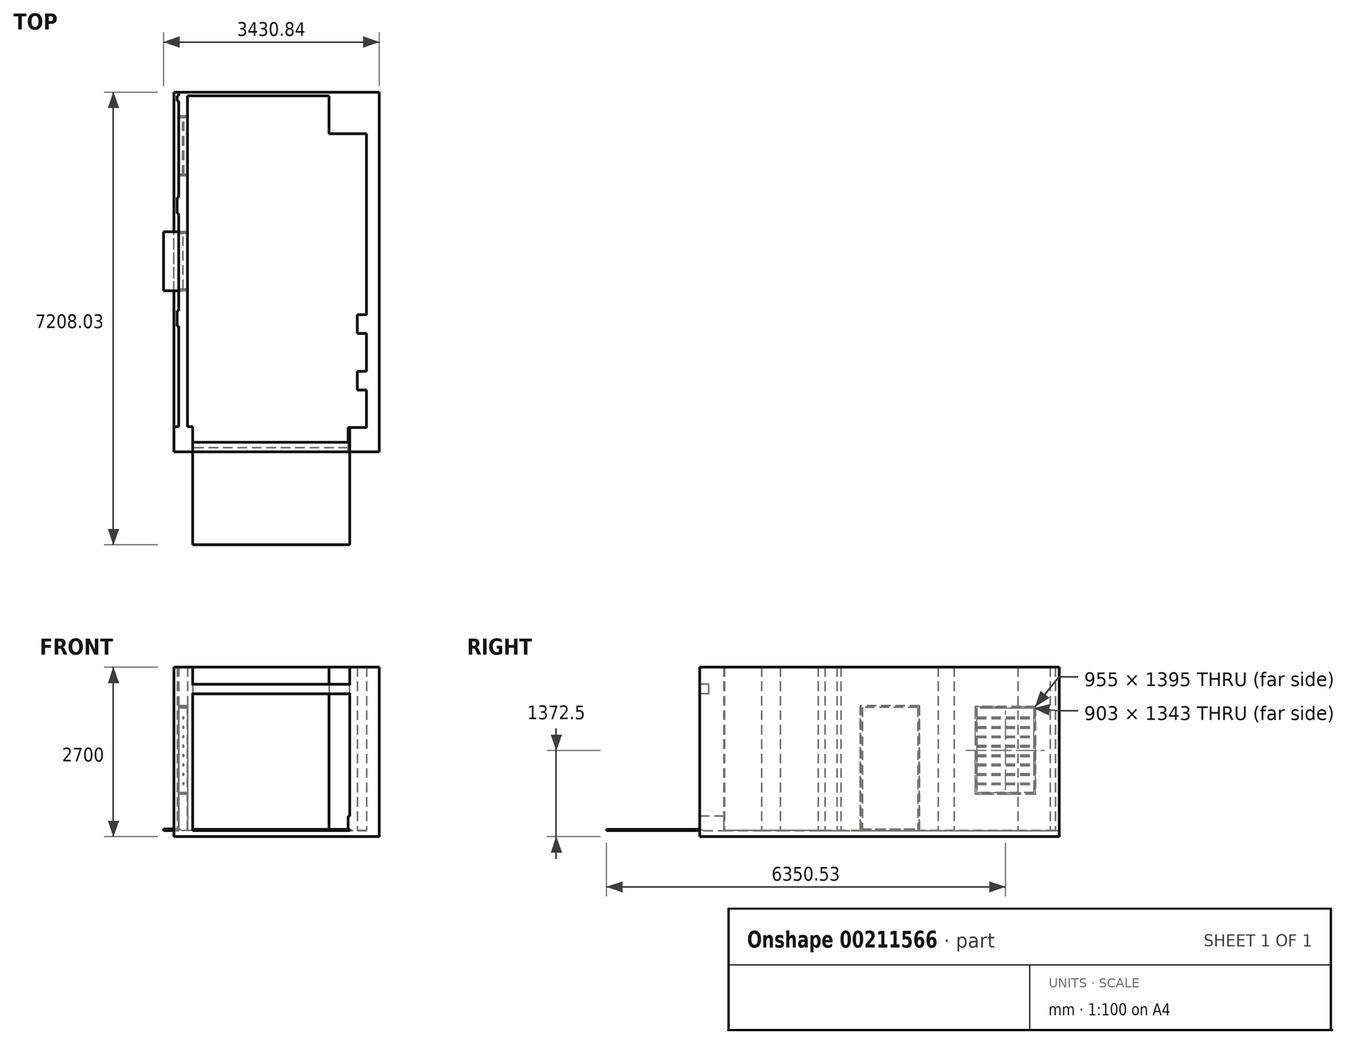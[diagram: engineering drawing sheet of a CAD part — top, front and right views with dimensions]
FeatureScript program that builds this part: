
annotation { "Feature Type Name" : "Feature", "Feature Type Description" : "" }
export const myFeature = defineFeature(function(context is Context, id is Id, definition is map)
    precondition{}
    {
        {
            var Q0;
            Q0=qCreatedBy(makeId("Top.planeOp"),FACE);
            var sketch = newSketch(context, id + "F0", { "sketchPlane" : qUnion([Q0])});
            skLineSegment(sketch, "E0.bottom", {"start": v(0, 0) * mm, "end": v(-270, 0) * mm});
            skLineSegment(sketch, "E0.top", {"start": v(0, 383) * mm, "end": v(-270, 383) * mm});
            skLineSegment(sketch, "E0.left", {"start": v(0, 0) * mm, "end": v(0, 383) * mm});
            skLineSegment(sketch, "E0.right", {"start": v(-270, 0) * mm, "end": v(-270, 383) * mm});
            skLineSegment(sketch, "E1.bottom", {"start": v(-2770, 0) * mm, "end": v(-3070, 0) * mm});
            skLineSegment(sketch, "E1.top", {"start": v(-2770, 395) * mm, "end": v(-3070, 395) * mm});
            skLineSegment(sketch, "E1.left", {"start": v(-2770, 0) * mm, "end": v(-2770, 395) * mm});
            skLineSegment(sketch, "E1.right", {"start": v(-3070, 0) * mm, "end": v(-3070, 395) * mm});
            skLineSegment(sketch, "E2.bottom", {"start": v(-3020, 1995) * mm, "end": v(-2850, 1995) * mm});
            skLineSegment(sketch, "E2.top", {"start": v(-3020, 2245) * mm, "end": v(-2850, 2245) * mm});
            skLineSegment(sketch, "E2.left", {"start": v(-3020, 1995) * mm, "end": v(-3020, 2245) * mm});
            skLineSegment(sketch, "E2.right", {"start": v(-2850, 1995) * mm, "end": v(-2850, 2245) * mm});
            skLineSegment(sketch, "E3", {"start": v(0, 383) * mm, "end": v(0, 983) * mm});
            skLineSegment(sketch, "E4.bottom", {"start": v(0, 983) * mm, "end": v(-150, 983) * mm});
            skLineSegment(sketch, "E4.top", {"start": v(0, 1283) * mm, "end": v(-150, 1283) * mm});
            skLineSegment(sketch, "E4.left", {"start": v(0, 983) * mm, "end": v(0, 1283) * mm});
            skLineSegment(sketch, "E4.right", {"start": v(-150, 983) * mm, "end": v(-150, 1283) * mm});
            skLineSegment(sketch, "E5.bottom", {"start": v(-2990, 1995) * mm, "end": v(-2850, 1995) * mm});
            skLineSegment(sketch, "E5.top", {"start": v(-2990, 395) * mm, "end": v(-2850, 395) * mm});
            skLineSegment(sketch, "E5.left", {"start": v(-2990, 1995) * mm, "end": v(-2990, 395) * mm});
            skLineSegment(sketch, "E5.right", {"start": v(-2850, 1995) * mm, "end": v(-2850, 395) * mm});
            skLineSegment(sketch, "E6.bottom", {"start": v(-2990, 2245) * mm, "end": v(-2850, 2245) * mm});
            skLineSegment(sketch, "E6.top", {"start": v(-2990, 3795) * mm, "end": v(-2850, 3795) * mm});
            skLineSegment(sketch, "E6.left", {"start": v(-2990, 2245) * mm, "end": v(-2990, 3795) * mm});
            skLineSegment(sketch, "E6.right", {"start": v(-2850, 2245) * mm, "end": v(-2850, 3795) * mm});
            skLineSegment(sketch, "E7.bottom", {"start": v(-3020, 3795) * mm, "end": v(-2850, 3795) * mm});
            skLineSegment(sketch, "E7.top", {"start": v(-3020, 4050) * mm, "end": v(-2850, 4050) * mm});
            skLineSegment(sketch, "E7.left", {"start": v(-3020, 3795) * mm, "end": v(-3020, 4050) * mm});
            skLineSegment(sketch, "E7.right", {"start": v(-2850, 3795) * mm, "end": v(-2850, 4050) * mm});
            skPoint(sketch, "E8.firstSnap0", {"position": v(-2935, 4050) * mm});
            skLineSegment(sketch, "E8.bottom", {"start": v(-2990, 4050) * mm, "end": v(-2850, 4050) * mm});
            skLineSegment(sketch, "E8.top", {"start": v(-2990, 5585) * mm, "end": v(-2850, 5585) * mm});
            skLineSegment(sketch, "E8.left", {"start": v(-2990, 4050) * mm, "end": v(-2990, 5585) * mm});
            skLineSegment(sketch, "E8.right", {"start": v(-2850, 4050) * mm, "end": v(-2850, 5585) * mm});
            skLineSegment(sketch, "E9.bottom", {"start": v(-3020, 5585) * mm, "end": v(-2850, 5585) * mm});
            skLineSegment(sketch, "E9.top", {"start": v(-3020, 5665) * mm, "end": v(-2850, 5665) * mm});
            skLineSegment(sketch, "E9.left", {"start": v(-3020, 5585) * mm, "end": v(-3020, 5665) * mm});
            skLineSegment(sketch, "E9.right", {"start": v(-2850, 5585) * mm, "end": v(-2850, 5665) * mm});
            skLineSegment(sketch, "E10", {"start": v(0, 1283) * mm, "end": v(0, 1883) * mm});
            skLineSegment(sketch, "E11.bottom", {"start": v(0, 1883) * mm, "end": v(-150, 1883) * mm});
            skLineSegment(sketch, "E11.top", {"start": v(0, 2183) * mm, "end": v(-150, 2183) * mm});
            skLineSegment(sketch, "E11.left", {"start": v(0, 1883) * mm, "end": v(0, 2183) * mm});
            skLineSegment(sketch, "E11.right", {"start": v(-150, 1883) * mm, "end": v(-150, 2183) * mm});
            skLineSegment(sketch, "E12", {"start": v(0, 2183) * mm, "end": v(0, 5665) * mm});
            skLineSegment(sketch, "E13", {"start": v(0, 5665) * mm, "end": v(-2850, 5665) * mm});
            skLineSegment(sketch, "E14.bottom", {"start": v(-600, 5665) * mm, "end": v(0, 5665) * mm});
            skLineSegment(sketch, "E14.top", {"start": v(-600, 5065) * mm, "end": v(0, 5065) * mm});
            skLineSegment(sketch, "E14.left", {"start": v(-600, 5665) * mm, "end": v(-600, 5065) * mm});
            skLineSegment(sketch, "E14.right", {"start": v(0, 5665) * mm, "end": v(0, 5065) * mm});
            skLineSegment(sketch, "E15.bottom", {"start": v(-2990, 5665) * mm, "end": v(200, 5665) * mm});
            skLineSegment(sketch, "E15.top", {"start": v(-2990, 5725) * mm, "end": v(200, 5725) * mm});
            skLineSegment(sketch, "E15.left", {"start": v(-2990, 5665) * mm, "end": v(-2990, 5725) * mm});
            skLineSegment(sketch, "E15.right", {"start": v(200, 5665) * mm, "end": v(200, 5725) * mm});
            skLineSegment(sketch, "E16.bottom", {"start": v(0, 5665) * mm, "end": v(200, 5665) * mm});
            skLineSegment(sketch, "E16.top", {"start": v(0, 0) * mm, "end": v(200, 0) * mm});
            skLineSegment(sketch, "E16.left", {"start": v(0, 5665) * mm, "end": v(0, 0) * mm});
            skLineSegment(sketch, "E16.right", {"start": v(200, 5665) * mm, "end": v(200, 0) * mm});
            skPoint(sketch, "E17", {"position": v(-2770, 0) * mm});
            skSolve(sketch);
        }
        {
            var Q0;
            Q0 = qSketchRegion(id + "F0", true);
            extrude(context, id + "F1", {"entities" : qUnion([Q0]), "offsetDistance" : 25 * mm, "depth" : 2600 * mm});
        }
        {
            var Q0;
            Q0=makeQuery(id+"F1.opExtrude","CAP_FACE",FACE,{"disambiguationData":[OSD([sQuery(id+"F0.wireOp",EDGE,"E0.bottom"),sQuery(id+"F0.wireOp",EDGE,"E0.top"),sQuery(id+"F0.wireOp",EDGE,"E0.right"),sQuery(id+"F0.wireOp",EDGE,"E1.bottom"),sQuery(id+"F0.wireOp",EDGE,"E1.top"),sQuery(id+"F0.wireOp",EDGE,"E1.left"),sQuery(id+"F0.wireOp",EDGE,"E1.right"),sQuery(id+"F0.wireOp",EDGE,"E2.bottom"),sQuery(id+"F0.wireOp",EDGE,"E2.top"),sQuery(id+"F0.wireOp",EDGE,"E2.left"),sQuery(id+"F0.wireOp",EDGE,"E2.right"),sQuery(id+"F0.wireOp",EDGE,"E4.bottom"),sQuery(id+"F0.wireOp",EDGE,"E4.top"),sQuery(id+"F0.wireOp",EDGE,"E4.right"),sQuery(id+"F0.wireOp",EDGE,"E5.left"),sQuery(id+"F0.wireOp",EDGE,"E5.right"),sQuery(id+"F0.wireOp",EDGE,"E6.left"),sQuery(id+"F0.wireOp",EDGE,"E6.right"),sQuery(id+"F0.wireOp",EDGE,"E7.bottom"),sQuery(id+"F0.wireOp",EDGE,"E7.top"),sQuery(id+"F0.wireOp",EDGE,"E7.left"),sQuery(id+"F0.wireOp",EDGE,"E7.right"),sQuery(id+"F0.wireOp",EDGE,"E8.left"),sQuery(id+"F0.wireOp",EDGE,"E8.right"),sQuery(id+"F0.wireOp",EDGE,"E9.bottom"),sQuery(id+"F0.wireOp",EDGE,"E9.top"),sQuery(id+"F0.wireOp",EDGE,"E9.left"),sQuery(id+"F0.wireOp",EDGE,"E9.right"),sQuery(id+"F0.wireOp",EDGE,"E11.bottom"),sQuery(id+"F0.wireOp",EDGE,"E11.top"),sQuery(id+"F0.wireOp",EDGE,"E11.right"),sQuery(id+"F0.wireOp",EDGE,"E14.top"),sQuery(id+"F0.wireOp",EDGE,"E14.left"),sQuery(id+"F0.wireOp",EDGE,"E15.bottom"),sQuery(id+"F0.wireOp",EDGE,"E15.top"),sQuery(id+"F0.wireOp",EDGE,"E15.left"),sQuery(id+"F0.wireOp",EDGE,"E15.right"),sQuery(id+"F0.wireOp",EDGE,"E16.top"),sQuery(id+"F0.wireOp",EDGE,"E16.left"),sQuery(id+"F0.wireOp",EDGE,"E16.right")])],"isStart":true});
            var sketch = newSketch(context, id + "F2", { "sketchPlane" : qUnion([Q0])});
            skLineSegment(sketch, "E18.bottom", {"start": v(-3070, 0) * mm, "end": v(200, 0) * mm});
            skLineSegment(sketch, "E18.top", {"start": v(-3070, -5725) * mm, "end": v(200, -5725) * mm});
            skLineSegment(sketch, "E18.left", {"start": v(-3070, 0) * mm, "end": v(-3070, -5725) * mm});
            skLineSegment(sketch, "E18.right", {"start": v(200, 0) * mm, "end": v(200, -5725) * mm});
            skSolve(sketch);
        }
        {
            var Q0;
            Q0 = qSketchRegion(id + "F2", true);
            extrude(context, id + "F3", {"entities" : qUnion([Q0]), "operationType" : NewBodyOperationType.ADD, "depth" : 100 * mm});
        }
        {
            var Q0;
            Q0=makeQuery(id+"F1.opExtrude","SWEPT_FACE",FACE,{"disambiguationData":[OSD([sQuery(id+"F0.wireOp",EDGE,"E1.left")])]});
            var sketch = newSketch(context, id + "F4", { "sketchPlane" : qUnion([Q0])});
            skLineSegment(sketch, "E19", {"start": v(0, 0) * mm, "end": v(60, 0) * mm});
            skLineSegment(sketch, "E20", {"start": v(60, 0) * mm, "end": v(0, 15) * mm});
            skLineSegment(sketch, "E21", {"start": v(0, 15) * mm, "end": v(-1483.03, 15) * mm});
            skLineSegment(sketch, "E22", {"start": v(-1483.03, 15) * mm, "end": v(-1483.03, 0) * mm});
            skLineSegment(sketch, "E23", {"start": v(-1483.03, 0) * mm, "end": v(0, 0) * mm});
            skSolve(sketch);
        }
        {
            var Q0;
            Q0 = qSketchRegion(id + "F4", true);
            var Q1;
            Q1=makeQuery(id+"F1.opExtrude","SWEPT_FACE",FACE,{"disambiguationData":[OSD([sQuery(id+"F0.wireOp",EDGE,"E0.right")])]});
            extrude(context, id + "F5", {"entities" : qUnion([Q0]), "operationType" : NewBodyOperationType.ADD, "endBound" : BoundingType.UP_TO_SURFACE, "endBoundEntityFace" : qUnion([Q1]), "depth" : 25 * mm});
        }
        {
            var Q0;
            Q0=makeQuery(id+"F1.opExtrude","SWEPT_FACE",FACE,{"disambiguationData":[OSD([sQuery(id+"F0.wireOp",EDGE,"E6.left")])]});
            var sketch = newSketch(context, id + "F6", { "sketchPlane" : qUnion([Q0])});
            skLineSegment(sketch, "E24.bottom", {"start": v(-3500, 0) * mm, "end": v(-2562, 0) * mm});
            skLineSegment(sketch, "E24.top", {"start": v(-3500, 1985) * mm, "end": v(-2562, 1985) * mm});
            skLineSegment(sketch, "E24.left", {"start": v(-3500, 0) * mm, "end": v(-3500, 1985) * mm});
            skLineSegment(sketch, "E24.right", {"start": v(-2562, 0) * mm, "end": v(-2562, 1985) * mm});
            skSolve(sketch);
        }
        {
            var Q0;
            Q0 = qSketchRegion(id + "F6", true);
            var Q1;
            Q1=makeQuery(id+"F1.opExtrude","SWEPT_FACE",FACE,{"disambiguationData":[OSD([sQuery(id+"F0.wireOp",EDGE,"E6.right")])]});
            extrude(context, id + "F7", {"entities" : qUnion([Q0]), "operationType" : NewBodyOperationType.REMOVE, "endBound" : BoundingType.UP_TO_SURFACE, "oppositeDirection" : true, "endBoundEntityFace" : qUnion([Q1]), "depth" : 25 * mm});
        }
        {
            var Q0;
            Q0=makeQuery(id+"F1.opExtrude","SWEPT_FACE",FACE,{"disambiguationData":[OSD([sQuery(id+"F0.wireOp",EDGE,"E8.left")])]});
            var sketch = newSketch(context, id + "F8", { "sketchPlane" : qUnion([Q0])});
            skLineSegment(sketch, "E25.bottom", {"start": v(-5345, 1970) * mm, "end": v(-4390, 1970) * mm});
            skLineSegment(sketch, "E25.top", {"start": v(-5345, 575) * mm, "end": v(-4390, 575) * mm});
            skLineSegment(sketch, "E25.left", {"start": v(-5345, 1970) * mm, "end": v(-5345, 575) * mm});
            skLineSegment(sketch, "E25.right", {"start": v(-4390, 1970) * mm, "end": v(-4390, 575) * mm});
            skSolve(sketch);
        }
        {
            var Q0;
            Q0 = qSketchRegion(id + "F8", true);
            var Q1;
            Q1=makeQuery(id+"F1.opExtrude","SWEPT_FACE",FACE,{"disambiguationData":[OSD([sQuery(id+"F0.wireOp",EDGE,"E8.right")])]});
            extrude(context, id + "F9", {"entities" : qUnion([Q0]), "operationType" : NewBodyOperationType.REMOVE, "endBound" : BoundingType.UP_TO_SURFACE, "oppositeDirection" : true, "endBoundEntityFace" : qUnion([Q1]), "depth" : 25 * mm});
        }
        {
            var Q0;
            Q0=makeQuery(id+"F7.boolean.opBoolean","COPY",FACE,{"derivedFrom":makeQuery(id+"F7.opExtrude","SWEPT_FACE",FACE,{"disambiguationData":[OSD([sQuery(id+"F6.wireOp",EDGE,"E24.left")])]})});
            var sketch = newSketch(context, id + "F10", { "sketchPlane" : qUnion([Q0])});
            skLineSegment(sketch, "E26", {"start": v(-2920, 0) * mm, "end": v(-2990, 25) * mm});
            skLineSegment(sketch, "E27", {"start": v(-2990, 25) * mm, "end": v(-3230.84, 25) * mm});
            skLineSegment(sketch, "E28", {"start": v(-3230.84, 25) * mm, "end": v(-3230.84, 0) * mm});
            skLineSegment(sketch, "E29", {"start": v(-3230.84, 0) * mm, "end": v(-2920, 0) * mm});
            skSolve(sketch);
        }
        {
            var Q0;
            Q0 = qSketchRegion(id + "F10", true);
            var Q1;
            Q1=makeQuery(id+"F7.boolean.opBoolean","COPY",FACE,{"derivedFrom":makeQuery(id+"F7.opExtrude","SWEPT_FACE",FACE,{"disambiguationData":[OSD([sQuery(id+"F6.wireOp",EDGE,"E24.right")])]})});
            extrude(context, id + "F11", {"entities" : qUnion([Q0]), "operationType" : NewBodyOperationType.ADD, "endBound" : BoundingType.UP_TO_SURFACE, "endBoundEntityFace" : qUnion([Q1]), "depth" : 25 * mm});
        }
        {
            var Q0;
            Q0=makeQuery(id+"F1.opExtrude","SWEPT_FACE",FACE,{"disambiguationData":[OSD([sQuery(id+"F0.wireOp",EDGE,"E0.right")])]});
            var sketch = newSketch(context, id + "F12", { "sketchPlane" : qUnion([Q0])});
            skLineSegment(sketch, "E30", {"start": v(-383, 0) * mm, "end": v(-383, 225) * mm});
            skLineSegment(sketch, "E31", {"start": v(-383, 225) * mm, "end": v(0, 225) * mm});
            skLineSegment(sketch, "E32", {"start": v(0, 225) * mm, "end": v(0, 15) * mm});
            skLineSegment(sketch, "E33", {"start": v(0, 15) * mm, "end": v(-60, 0) * mm});
            skLineSegment(sketch, "E34", {"start": v(-60, 0) * mm, "end": v(-383, 0) * mm});
            skSolve(sketch);
        }
        {
            var Q0;
            Q0 = qSketchRegion(id + "F12", true);
            extrude(context, id + "F13", {"entities" : qUnion([Q0]), "operationType" : NewBodyOperationType.ADD, "depth" : 25 * mm});
        }
        {
            var Q0;
            Q0=makeQuery(id+"F1.opExtrude","SWEPT_FACE",FACE,{"disambiguationData":[OSD([sQuery(id+"F0.wireOp",EDGE,"E1.left")])]});
            var sketch = newSketch(context, id + "F14", { "sketchPlane" : qUnion([Q0])});
            skLineSegment(sketch, "E35.bottom", {"start": v(10, 2325) * mm, "end": v(138, 2325) * mm});
            skLineSegment(sketch, "E35.top", {"start": v(10, 2177) * mm, "end": v(138, 2177) * mm});
            skLineSegment(sketch, "E35.left", {"start": v(0, 2315) * mm, "end": v(0, 2187) * mm});
            skLineSegment(sketch, "E35.right", {"start": v(148, 2315) * mm, "end": v(148, 2187) * mm});
            skPoint(sketch, "E36.visualSharp", {"position": v(148, 2325) * mm});
            skArc(sketch, "E36.filletArc", {"start": v(148, 2315) * mm, "mid": v(145.07, 2322.07) * mm, "end": v(138, 2325) * mm});
            skPoint(sketch, "E37.visualSharp", {"position": v(148, 2177) * mm});
            skArc(sketch, "E37.filletArc", {"start": v(138, 2177) * mm, "mid": v(145.07, 2179.93) * mm, "end": v(148, 2187) * mm});
            skPoint(sketch, "E38.visualSharp", {"position": v(0, 2325) * mm});
            skArc(sketch, "E38.filletArc", {"start": v(10, 2325) * mm, "mid": v(2.93, 2322.07) * mm, "end": v(0, 2315) * mm});
            skPoint(sketch, "E39.visualSharp", {"position": v(0, 2177) * mm});
            skArc(sketch, "E39.filletArc", {"start": v(0, 2187) * mm, "mid": v(2.93, 2179.93) * mm, "end": v(10, 2177) * mm});
            skSolve(sketch);
        }
        {
            var Q0;
            Q0 = qSketchRegion(id + "F14", true);
            var Q1;
            Q1=makeQuery(id+"F1.opExtrude","SWEPT_FACE",FACE,{"disambiguationData":[OSD([sQuery(id+"F0.wireOp",EDGE,"E0.right")])]});
            extrude(context, id + "F15", {"entities" : qUnion([Q0]), "operationType" : NewBodyOperationType.ADD, "endBound" : BoundingType.UP_TO_SURFACE, "endBoundEntityFace" : qUnion([Q1]), "depth" : 25 * mm});
        }
        {
            var Q0;
            Q0=makeQuery(id+"F1.opExtrude","SWEPT_FACE",FACE,{"disambiguationData":[OSD([sQuery(id+"F0.wireOp",EDGE,"E6.left")])]});
            var sketch = newSketch(context, id + "F16", { "sketchPlane" : qUnion([Q0])});
            skLineSegment(sketch, "E40.bottom", {"start": v(-3499, 1984) * mm, "end": v(-2563, 1984) * mm});
            skLineSegment(sketch, "E40.top", {"start": v(-3499, 1959) * mm, "end": v(-2563, 1959) * mm});
            skLineSegment(sketch, "E40.left", {"start": v(-3499, 1984) * mm, "end": v(-3499, 1959) * mm});
            skLineSegment(sketch, "E40.right", {"start": v(-2563, 1984) * mm, "end": v(-2563, 1959) * mm});
            skLineSegment(sketch, "E41.bottom", {"start": v(-3499, 1959) * mm, "end": v(-3474, 1959) * mm});
            skLineSegment(sketch, "E41.top", {"start": v(-3499, 0) * mm, "end": v(-3474, 0) * mm});
            skLineSegment(sketch, "E41.left", {"start": v(-3499, 1959) * mm, "end": v(-3499, 0) * mm});
            skLineSegment(sketch, "E41.right", {"start": v(-3474, 1959) * mm, "end": v(-3474, 0) * mm});
            skLineSegment(sketch, "E42.bottom", {"start": v(-2563, 1959) * mm, "end": v(-2588, 1959) * mm});
            skLineSegment(sketch, "E42.top", {"start": v(-2563, 0) * mm, "end": v(-2588, 0) * mm});
            skLineSegment(sketch, "E42.left", {"start": v(-2563, 1959) * mm, "end": v(-2563, 0) * mm});
            skLineSegment(sketch, "E42.right", {"start": v(-2588, 1959) * mm, "end": v(-2588, 0) * mm});
            skSolve(sketch);
        }
        {
            var Q0;
            Q0 = qSketchRegion(id + "F16", true);
            var Q1;
            Q1=makeQuery(id+"F1.opExtrude","SWEPT_FACE",FACE,{"disambiguationData":[OSD([sQuery(id+"F0.wireOp",EDGE,"E2.right"),sQuery(id+"F0.wireOp",EDGE,"E5.right"),sQuery(id+"F0.wireOp",EDGE,"E6.right"),sQuery(id+"F0.wireOp",EDGE,"E7.right"),sQuery(id+"F0.wireOp",EDGE,"E8.right"),sQuery(id+"F0.wireOp",EDGE,"E9.right")])]});
            extrude(context, id + "F17", {"entities" : qUnion([Q0]), "operationType" : NewBodyOperationType.ADD, "endBound" : BoundingType.UP_TO_SURFACE, "oppositeDirection" : true, "endBoundEntityFace" : qUnion([Q1]), "depth" : 144 * mm});
        }
        {
            var Q0;
            Q0=makeQuery(id+"F1.opExtrude","SWEPT_FACE",FACE,{"disambiguationData":[OSD([sQuery(id+"F0.wireOp",EDGE,"E8.left")])]});
            var sketch = newSketch(context, id + "F18", { "sketchPlane" : qUnion([Q0])});
            skLineSegment(sketch, "E43.bottom", {"start": v(-5344, 1969) * mm, "end": v(-4391, 1969) * mm});
            skLineSegment(sketch, "E43.top", {"start": v(-5344, 1944) * mm, "end": v(-4391, 1944) * mm});
            skLineSegment(sketch, "E43.left", {"start": v(-5344, 1969) * mm, "end": v(-5344, 1944) * mm});
            skLineSegment(sketch, "E43.right", {"start": v(-4391, 1969) * mm, "end": v(-4391, 1944) * mm});
            skLineSegment(sketch, "E44.bottom", {"start": v(-5344, 1944) * mm, "end": v(-5319, 1944) * mm});
            skLineSegment(sketch, "E44.top", {"start": v(-5344, 576) * mm, "end": v(-5319, 576) * mm});
            skLineSegment(sketch, "E44.left", {"start": v(-5344, 1944) * mm, "end": v(-5344, 576) * mm});
            skLineSegment(sketch, "E44.right", {"start": v(-5319, 1944) * mm, "end": v(-5319, 576) * mm});
            skLineSegment(sketch, "E45.bottom", {"start": v(-5319, 576) * mm, "end": v(-4391, 576) * mm});
            skLineSegment(sketch, "E45.top", {"start": v(-5319, 601) * mm, "end": v(-4391, 601) * mm});
            skLineSegment(sketch, "E45.left", {"start": v(-5319, 576) * mm, "end": v(-5319, 601) * mm});
            skLineSegment(sketch, "E45.right", {"start": v(-4391, 576) * mm, "end": v(-4391, 601) * mm});
            skLineSegment(sketch, "E46.bottom", {"start": v(-4391, 1944) * mm, "end": v(-4416, 1944) * mm});
            skLineSegment(sketch, "E46.top", {"start": v(-4391, 601) * mm, "end": v(-4416, 601) * mm});
            skLineSegment(sketch, "E46.left", {"start": v(-4391, 1944) * mm, "end": v(-4391, 601) * mm});
            skLineSegment(sketch, "E46.right", {"start": v(-4416, 1944) * mm, "end": v(-4416, 601) * mm});
            skSolve(sketch);
        }
        {
            var Q0;
            Q0 = qSketchRegion(id + "F18", true);
            var Q1;
            Q1=makeQuery(id+"F1.opExtrude","SWEPT_FACE",FACE,{"disambiguationData":[OSD([sQuery(id+"F0.wireOp",EDGE,"E2.right"),sQuery(id+"F0.wireOp",EDGE,"E5.right"),sQuery(id+"F0.wireOp",EDGE,"E6.right"),sQuery(id+"F0.wireOp",EDGE,"E7.right"),sQuery(id+"F0.wireOp",EDGE,"E8.right"),sQuery(id+"F0.wireOp",EDGE,"E9.right")])]});
            extrude(context, id + "F19", {"entities" : qUnion([Q0]), "endBound" : BoundingType.UP_TO_SURFACE, "oppositeDirection" : true, "endBoundEntityFace" : qUnion([Q1]), "depth" : 25 * mm});
        }
        {
            var Q0;
            Q0=makeQuery(id+"F19.opExtrude","SWEPT_FACE",FACE,{"disambiguationData":[OSD([sQuery(id+"F18.wireOp",EDGE,"E44.right")])]});
            var sketch = newSketch(context, id + "F20", { "sketchPlane" : qUnion([Q0])});
            skCircle(sketch, "E47", {"center": v(-2920, 743.2) * mm, "radius": 11.82 * mm});
            skPoint(sketch, "E47.centerSnap0", {"position": v(-2920, 601) * mm});
            skCircle(sketch, "E48.0.1.0", {"center": v(-2920, 893.2) * mm, "radius": 11.82 * mm});
            skCircle(sketch, "E48.0.2.0", {"center": v(-2920, 1043.2) * mm, "radius": 11.82 * mm});
            skCircle(sketch, "E48.0.3.0", {"center": v(-2920, 1193.2) * mm, "radius": 11.82 * mm});
            skCircle(sketch, "E48.0.4.0", {"center": v(-2920, 1343.2) * mm, "radius": 11.82 * mm});
            skCircle(sketch, "E48.0.5.0", {"center": v(-2920, 1493.2) * mm, "radius": 11.82 * mm});
            skCircle(sketch, "E48.0.6.0", {"center": v(-2920, 1643.2) * mm, "radius": 11.82 * mm});
            skCircle(sketch, "E48.0.7.0", {"center": v(-2920, 1793.2) * mm, "radius": 11.82 * mm});
            skLineSegment(sketch, "E48.direction1", {"start": v(-2920, 743.2) * mm, "end": v(-2895, 743.2) * mm, "construction": true});
            skLineSegment(sketch, "E48.direction2", {"start": v(-2920, 743.2) * mm, "end": v(-2920, 893.2) * mm, "construction": true});
            skSolve(sketch);
        }
        {
            var Q0;
            Q0 = qSketchRegion(id + "F20", true);
            var Q1;
            Q1=makeQuery(id+"F19.opExtrude","SWEPT_FACE",FACE,{"disambiguationData":[OSD([sQuery(id+"F18.wireOp",EDGE,"E46.right")])]});
            extrude(context, id + "F21", {"entities" : qUnion([Q0]), "endBound" : BoundingType.UP_TO_SURFACE, "endBoundEntityFace" : qUnion([Q1]), "depth" : 25 * mm});
        }
    });
